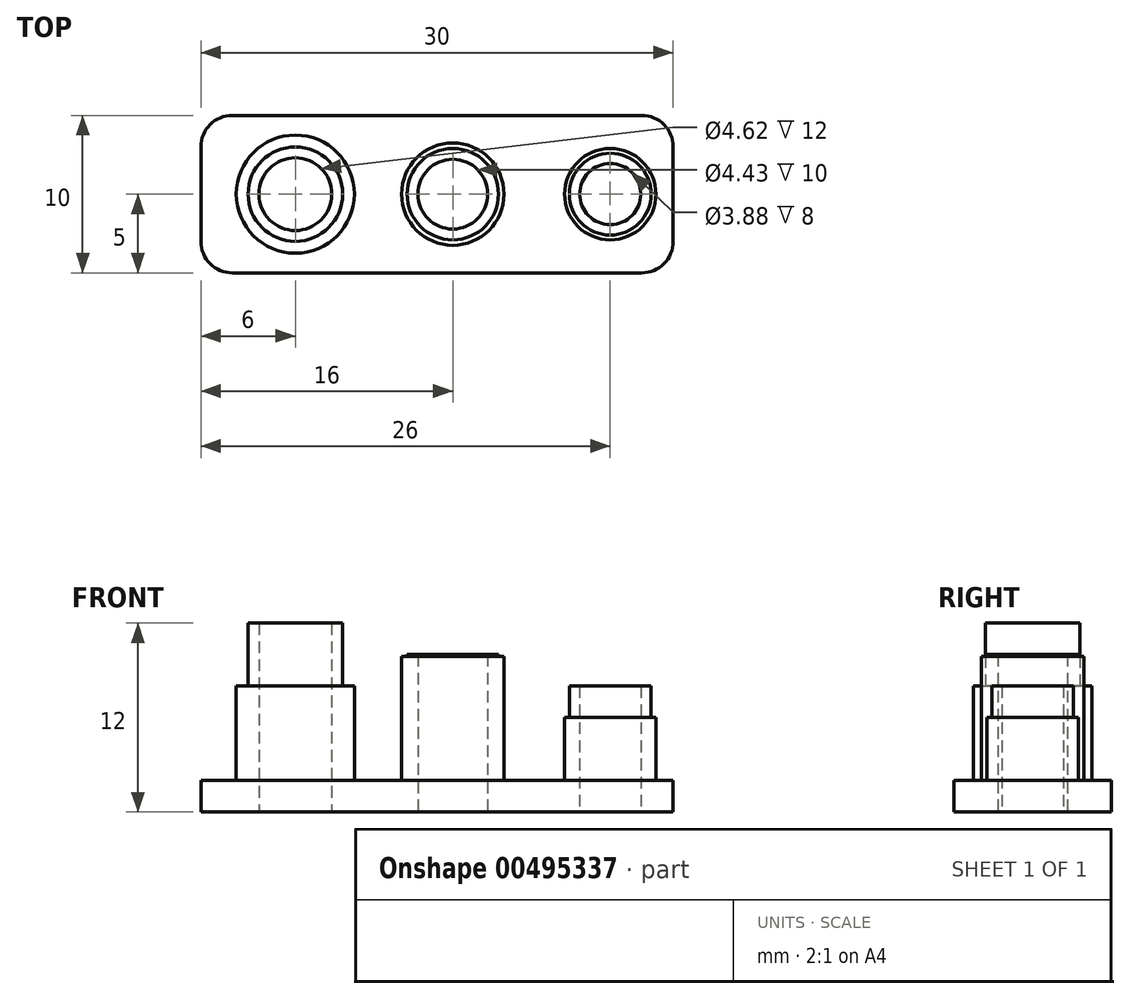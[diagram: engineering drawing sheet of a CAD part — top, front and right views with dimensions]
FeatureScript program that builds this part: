
annotation { "Feature Type Name" : "Feature", "Feature Type Description" : "" }
export const myFeature = defineFeature(function(context is Context, id is Id, definition is map)
    precondition{}
    {
        {
            var Q0;
            Q0=qCreatedBy(makeId("Top.planeOp"),FACE);
            var sketch = newSketch(context, id + "F0", { "sketchPlane" : qUnion([Q0])});
            skLineSegment(sketch, "E0.bottom", {"start": v(12, -5) * mm, "end": v(-12, -5) * mm});
            skLineSegment(sketch, "E0.top", {"start": v(12, 5) * mm, "end": v(-12, 5) * mm});
            skLineSegment(sketch, "E0.left", {"start": v(14, -3) * mm, "end": v(14, 3) * mm});
            skLineSegment(sketch, "E0.right", {"start": v(-14, -3) * mm, "end": v(-14, 3) * mm});
            skPoint(sketch, "E1", {"position": v(-10, 0) * mm});
            skPoint(sketch, "E2", {"position": v(0, 0) * mm});
            skPoint(sketch, "E3", {"position": v(10, 0) * mm});
            skCircle(sketch, "E4", {"center": v(-10, 0) * mm, "radius": 3 * mm});
            skCircle(sketch, "E5", {"center": v(-10, 0) * mm, "radius": 2.31 * mm});
            skCircle(sketch, "E6", {"center": v(0, 0) * mm, "radius": 2.9 * mm});
            skCircle(sketch, "E7", {"center": v(0, 0) * mm, "radius": 2.21 * mm});
            skCircle(sketch, "E8", {"center": v(10, 0) * mm, "radius": 2.6 * mm});
            skCircle(sketch, "E9", {"center": v(10, 0) * mm, "radius": 1.94 * mm});
            skPoint(sketch, "E10.visualSharp", {"position": v(-14, 5) * mm});
            skArc(sketch, "E10.filletArc", {"start": v(-12, 5) * mm, "mid": v(-13.41, 4.41) * mm, "end": v(-14, 3) * mm});
            skPoint(sketch, "E11.visualSharp", {"position": v(-14, -5) * mm});
            skArc(sketch, "E11.filletArc", {"start": v(-14, -3) * mm, "mid": v(-13.41, -4.41) * mm, "end": v(-12, -5) * mm});
            skPoint(sketch, "E12.visualSharp", {"position": v(14, -5) * mm});
            skArc(sketch, "E12.filletArc", {"start": v(12, -5) * mm, "mid": v(13.41, -4.41) * mm, "end": v(14, -3) * mm});
            skPoint(sketch, "E13.visualSharp", {"position": v(14, 5) * mm});
            skArc(sketch, "E13.filletArc", {"start": v(14, 3) * mm, "mid": v(13.41, 4.41) * mm, "end": v(12, 5) * mm});
            skSolve(sketch);
        }
        {
            var Q0;
            Q0=makeQuery(id+"F0.imprint","IMPRINT",FACE,{"disambiguationData":[TD([[makeQuery(id+"F0.imprint","IMPRINT",EDGE,{"derivedFrom":sQuery(id+"F0.wireOp",EDGE,"E0.bottom")}),-1.0]])]});
            extrude(context, id + "F1", {"entities" : qUnion([Q0]), "offsetDistance" : 25 * mm, "depth" : 2 * mm});
        }
        {
            var Q0;
            Q0=makeQuery(id+"F0.imprint","IMPRINT",FACE,{"disambiguationData":[TD([[makeQuery(id+"F0.imprint","IMPRINT",EDGE,{"derivedFrom":sQuery(id+"F0.wireOp",EDGE,"E4")}),1.0]])]});
            extrude(context, id + "F2", {"entities" : qUnion([Q0]), "operationType" : NewBodyOperationType.ADD, "depth" : 12 * mm});
        }
        {
            var Q0;
            Q0=makeQuery(id+"F0.imprint","IMPRINT",FACE,{"disambiguationData":[TD([[makeQuery(id+"F0.imprint","IMPRINT",EDGE,{"derivedFrom":sQuery(id+"F0.wireOp",EDGE,"E6")}),1.0]])]});
            extrude(context, id + "F3", {"entities" : qUnion([Q0]), "operationType" : NewBodyOperationType.ADD, "depth" : 10 * mm});
        }
        {
            var Q0;
            Q0=makeQuery(id+"F0.imprint","IMPRINT",FACE,{"disambiguationData":[TD([[makeQuery(id+"F0.imprint","IMPRINT",EDGE,{"derivedFrom":sQuery(id+"F0.wireOp",EDGE,"E8")}),1.0]])]});
            extrude(context, id + "F4", {"entities" : qUnion([Q0]), "operationType" : NewBodyOperationType.ADD, "depth" : 8 * mm});
        }
        {
            var Q0;
            Q0=qCreatedBy(makeId("Top.planeOp"),FACE);
            var sketch = newSketch(context, id + "F5", { "sketchPlane" : qUnion([Q0])});
            skLineSegment(sketch, "E14.0", {"start": v(12, -5) * mm, "end": v(-12, -5) * mm});
            skLineSegment(sketch, "E14.1", {"start": v(12, 5) * mm, "end": v(-12, 5) * mm});
            skLineSegment(sketch, "E14.2", {"start": v(14, -3) * mm, "end": v(14, 3) * mm});
            skPoint(sketch, "E15.0", {"position": v(-12, 3) * mm});
            skPoint(sketch, "E16.0", {"position": v(-12, -3) * mm});
            skPoint(sketch, "E17.0", {"position": v(12, -3) * mm});
            skPoint(sketch, "E18.0", {"position": v(12, 3) * mm});
            skArc(sketch, "E19", {"start": v(12, 5) * mm, "mid": v(13.41, 4.41) * mm, "end": v(14, 3) * mm});
            skArc(sketch, "E20", {"start": v(14, -3) * mm, "mid": v(13.41, -4.41) * mm, "end": v(12, -5) * mm});
            skPoint(sketch, "E21", {"position": v(10, 0) * mm});
            skPoint(sketch, "E22", {"position": v(-10, 0) * mm});
            skCircle(sketch, "E23", {"center": v(10, 0) * mm, "radius": 2.9 * mm});
            skCircle(sketch, "E24", {"center": v(10, 0) * mm, "radius": 2.21 * mm});
            skCircle(sketch, "E25", {"center": v(0, 0) * mm, "radius": 2.54 * mm});
            skCircle(sketch, "E26", {"center": v(0, 0) * mm, "radius": 3.25 * mm});
            skCircle(sketch, "E27", {"center": v(-10, 0) * mm, "radius": 2.83 * mm});
            skCircle(sketch, "E28", {"center": v(-10, 0) * mm, "radius": 3.75 * mm});
            skLineSegment(sketch, "E29", {"start": v(-12, 5) * mm, "end": v(-14, 5) * mm});
            skLineSegment(sketch, "E30", {"start": v(-12, -5) * mm, "end": v(-14, -5) * mm});
            skPoint(sketch, "E31", {"position": v(-14, 3) * mm});
            skPoint(sketch, "E32", {"position": v(-14, -3) * mm});
            skArc(sketch, "E33", {"start": v(-14, 5) * mm, "mid": v(-15.41, 4.41) * mm, "end": v(-16, 3) * mm});
            skArc(sketch, "E34", {"start": v(-14, -5) * mm, "mid": v(-15.41, -4.41) * mm, "end": v(-16, -3) * mm});
            skLineSegment(sketch, "E35", {"start": v(-16, 3) * mm, "end": v(-16, -3) * mm});
            skSolve(sketch);
        }
        {
            var Q0;
            Q0 = qSketchRegion(id + "F5", true);
            extrude(context, id + "F6", {"entities" : qUnion([Q0]), "depth" : 2 * mm, "offsetDistance" : 25 * mm});
        }
        {
            var Q0;
            Q0=makeQuery(id+"F5.imprint","IMPRINT",FACE,{"disambiguationData":[TD([[makeQuery(id+"F5.imprint","IMPRINT",EDGE,{"derivedFrom":sQuery(id+"F5.wireOp",EDGE,"E23")}),1.0]])]});
            extrude(context, id + "F7", {"entities" : qUnion([Q0]), "operationType" : NewBodyOperationType.ADD, "depth" : 6 * mm, "offsetDistance" : 25 * mm});
        }
        {
            var Q0;
            Q0=makeQuery(id+"F5.imprint","IMPRINT",FACE,{"disambiguationData":[TD([[makeQuery(id+"F5.imprint","IMPRINT",EDGE,{"derivedFrom":sQuery(id+"F5.wireOp",EDGE,"E25")}),-1.0]])]});
            extrude(context, id + "F8", {"entities" : qUnion([Q0]), "operationType" : NewBodyOperationType.ADD, "depth" : 9.9 * mm, "offsetDistance" : 25 * mm});
        }
        {
            var Q0;
            Q0=makeQuery(id+"F5.imprint","IMPRINT",FACE,{"disambiguationData":[TD([[makeQuery(id+"F5.imprint","IMPRINT",EDGE,{"derivedFrom":sQuery(id+"F5.wireOp",EDGE,"E27")}),-1.0]])]});
            extrude(context, id + "F9", {"entities" : qUnion([Q0]), "operationType" : NewBodyOperationType.ADD, "depth" : 8 * mm, "offsetDistance" : 25 * mm});
        }
    });
